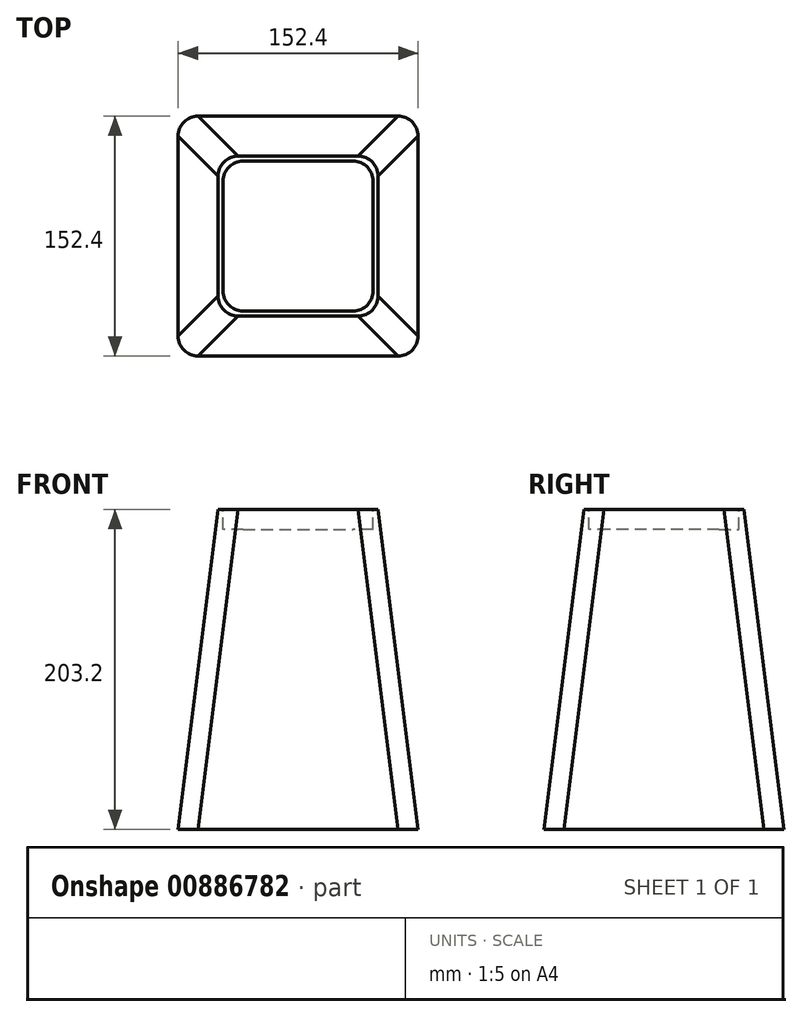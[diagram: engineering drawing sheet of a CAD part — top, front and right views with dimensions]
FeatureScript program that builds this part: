
annotation { "Feature Type Name" : "Feature", "Feature Type Description" : "" }
export const myFeature = defineFeature(function(context is Context, id is Id, definition is map)
    precondition{}
    {
        {
            var Q0;
            Q0=qCreatedBy(makeId("Top.planeOp"),FACE);
            var sketch = newSketch(context, id + "F0", { "sketchPlane" : qUnion([Q0])});
            skLineSegment(sketch, "E0.bottom", {"start": v(-63.5, 76.2) * mm, "end": v(63.5, 76.2) * mm});
            skLineSegment(sketch, "E0.top", {"start": v(-63.5, -76.2) * mm, "end": v(63.5, -76.2) * mm});
            skLineSegment(sketch, "E0.left", {"start": v(-76.2, 63.5) * mm, "end": v(-76.2, -63.5) * mm});
            skLineSegment(sketch, "E0.right", {"start": v(76.2, 63.5) * mm, "end": v(76.2, -63.5) * mm});
            skPoint(sketch, "E0.middle", {"position": v(0, 0) * mm});
            skPoint(sketch, "E1.visualSharp", {"position": v(-76.2, -76.2) * mm});
            skArc(sketch, "E1.filletArc", {"start": v(-76.2, -63.5) * mm, "mid": v(-72.48, -72.48) * mm, "end": v(-63.5, -76.2) * mm});
            skPoint(sketch, "E2.visualSharp", {"position": v(-76.2, 76.2) * mm});
            skArc(sketch, "E2.filletArc", {"start": v(-63.5, 76.2) * mm, "mid": v(-72.48, 72.48) * mm, "end": v(-76.2, 63.5) * mm});
            skPoint(sketch, "E3.visualSharp", {"position": v(76.2, 76.2) * mm});
            skArc(sketch, "E3.filletArc", {"start": v(76.2, 63.5) * mm, "mid": v(72.48, 72.48) * mm, "end": v(63.5, 76.2) * mm});
            skPoint(sketch, "E4.visualSharp", {"position": v(76.2, -76.2) * mm});
            skArc(sketch, "E4.filletArc", {"start": v(63.5, -76.2) * mm, "mid": v(72.48, -72.48) * mm, "end": v(76.2, -63.5) * mm});
            skSolve(sketch);
        }
        {
            var Q0;
            Q0=qCreatedBy(makeId("Top.planeOp"),FACE);
            cPlane(context, id + "F1", {"entities" : qUnion([Q0]), "cplaneType" : CPlaneType.OFFSET, "offset" : 203.2 * mm, "width" : 152.4 * mm, "height" : 152.4 * mm});
        }
        {
            var Q0;
            Q0=qCreatedBy(id+"F1.planeOp",FACE);
            var sketch = newSketch(context, id + "F2", { "sketchPlane" : qUnion([Q0])});
            skLineSegment(sketch, "E5.bottom", {"start": v(-38.1, 50.8) * mm, "end": v(38.1, 50.8) * mm});
            skLineSegment(sketch, "E5.top", {"start": v(-38.1, -50.8) * mm, "end": v(38.1, -50.8) * mm});
            skLineSegment(sketch, "E5.left", {"start": v(-50.8, 38.1) * mm, "end": v(-50.8, -38.1) * mm});
            skLineSegment(sketch, "E5.right", {"start": v(50.8, 38.1) * mm, "end": v(50.8, -38.1) * mm});
            skPoint(sketch, "E5.middle", {"position": v(0, 0) * mm});
            skPoint(sketch, "E6.visualSharp", {"position": v(-50.8, -50.8) * mm});
            skArc(sketch, "E6.filletArc", {"start": v(-50.8, -38.1) * mm, "mid": v(-47.08, -47.08) * mm, "end": v(-38.1, -50.8) * mm});
            skPoint(sketch, "E7.visualSharp", {"position": v(-50.8, 50.8) * mm});
            skArc(sketch, "E7.filletArc", {"start": v(-38.1, 50.8) * mm, "mid": v(-47.08, 47.08) * mm, "end": v(-50.8, 38.1) * mm});
            skPoint(sketch, "E8.visualSharp", {"position": v(50.8, 50.8) * mm});
            skArc(sketch, "E8.filletArc", {"start": v(50.8, 38.1) * mm, "mid": v(47.08, 47.08) * mm, "end": v(38.1, 50.8) * mm});
            skPoint(sketch, "E9.visualSharp", {"position": v(50.8, -50.8) * mm});
            skArc(sketch, "E9.filletArc", {"start": v(38.1, -50.8) * mm, "mid": v(47.08, -47.08) * mm, "end": v(50.8, -38.1) * mm});
            skSolve(sketch);
        }
        {
            var Q0;
            Q0=makeQuery(id+"F0.imprint","IMPRINT",FACE,{"disambiguationData":[TD([[makeQuery(id+"F0.imprint","IMPRINT",EDGE,{"derivedFrom":sQuery(id+"F0.wireOp",EDGE,"E0.bottom")}),-1.0]])]});
            var Q1;
            Q1=makeQuery(id+"F2.imprint","IMPRINT",FACE,{"disambiguationData":[TD([[makeQuery(id+"F2.imprint","IMPRINT",EDGE,{"derivedFrom":sQuery(id+"F2.wireOp",EDGE,"E5.bottom")}),-1.0]])]});
            loft(context, id + "F3", {"sheetProfilesArray" : [{ "sheetProfileEntities" : qUnion([Q0]) }, { "sheetProfileEntities" : qUnion([Q1]) }]});
        }
        {
            var Q0;
            Q0=makeQuery(id+"F3.opLoft","CAP_FACE",FACE,{"disambiguationData":[OSD([makeQuery(id+"F2.imprint","IMPRINT",FACE,{"disambiguationData":[TD([[makeQuery(id+"F2.imprint","IMPRINT",EDGE,{"derivedFrom":sQuery(id+"F2.wireOp",EDGE,"E5.bottom")}),-1.0]])]})])],"isStart":true});
            var sketch = newSketch(context, id + "F4", { "sketchPlane" : qUnion([Q0])});
            skLineSegment(sketch, "E10.bottom", {"start": v(-34.92, 47.63) * mm, "end": v(34.93, 47.63) * mm});
            skLineSegment(sketch, "E10.top", {"start": v(-34.92, -47.63) * mm, "end": v(34.93, -47.63) * mm});
            skLineSegment(sketch, "E10.left", {"start": v(-47.62, 34.93) * mm, "end": v(-47.62, -34.93) * mm});
            skLineSegment(sketch, "E10.right", {"start": v(47.63, 34.93) * mm, "end": v(47.63, -34.93) * mm});
            skPoint(sketch, "E10.middle", {"position": v(0, 0) * mm});
            skPoint(sketch, "E11.visualSharp", {"position": v(-47.62, 47.63) * mm});
            skArc(sketch, "E11.filletArc", {"start": v(-34.92, 47.63) * mm, "mid": v(-43.9, 43.9) * mm, "end": v(-47.63, 34.93) * mm});
            skPoint(sketch, "E12.visualSharp", {"position": v(47.63, 47.63) * mm});
            skArc(sketch, "E12.filletArc", {"start": v(47.63, 34.93) * mm, "mid": v(43.9, 43.9) * mm, "end": v(34.93, 47.63) * mm});
            skPoint(sketch, "E13.visualSharp", {"position": v(47.63, -47.63) * mm});
            skArc(sketch, "E13.filletArc", {"start": v(34.93, -47.63) * mm, "mid": v(43.9, -43.9) * mm, "end": v(47.63, -34.93) * mm});
            skPoint(sketch, "E14.visualSharp", {"position": v(-47.62, -47.63) * mm});
            skArc(sketch, "E14.filletArc", {"start": v(-47.63, -34.93) * mm, "mid": v(-43.9, -43.9) * mm, "end": v(-34.92, -47.63) * mm});
            skSolve(sketch);
        }
        {
            var Q0;
            Q0 = qSketchRegion(id + "F4", true);
            extrude(context, id + "F5", {"entities" : qUnion([Q0]), "operationType" : NewBodyOperationType.REMOVE, "oppositeDirection" : true, "depth" : 12.7 * mm, "offsetDistance" : 25.4 * mm});
        }
    });
